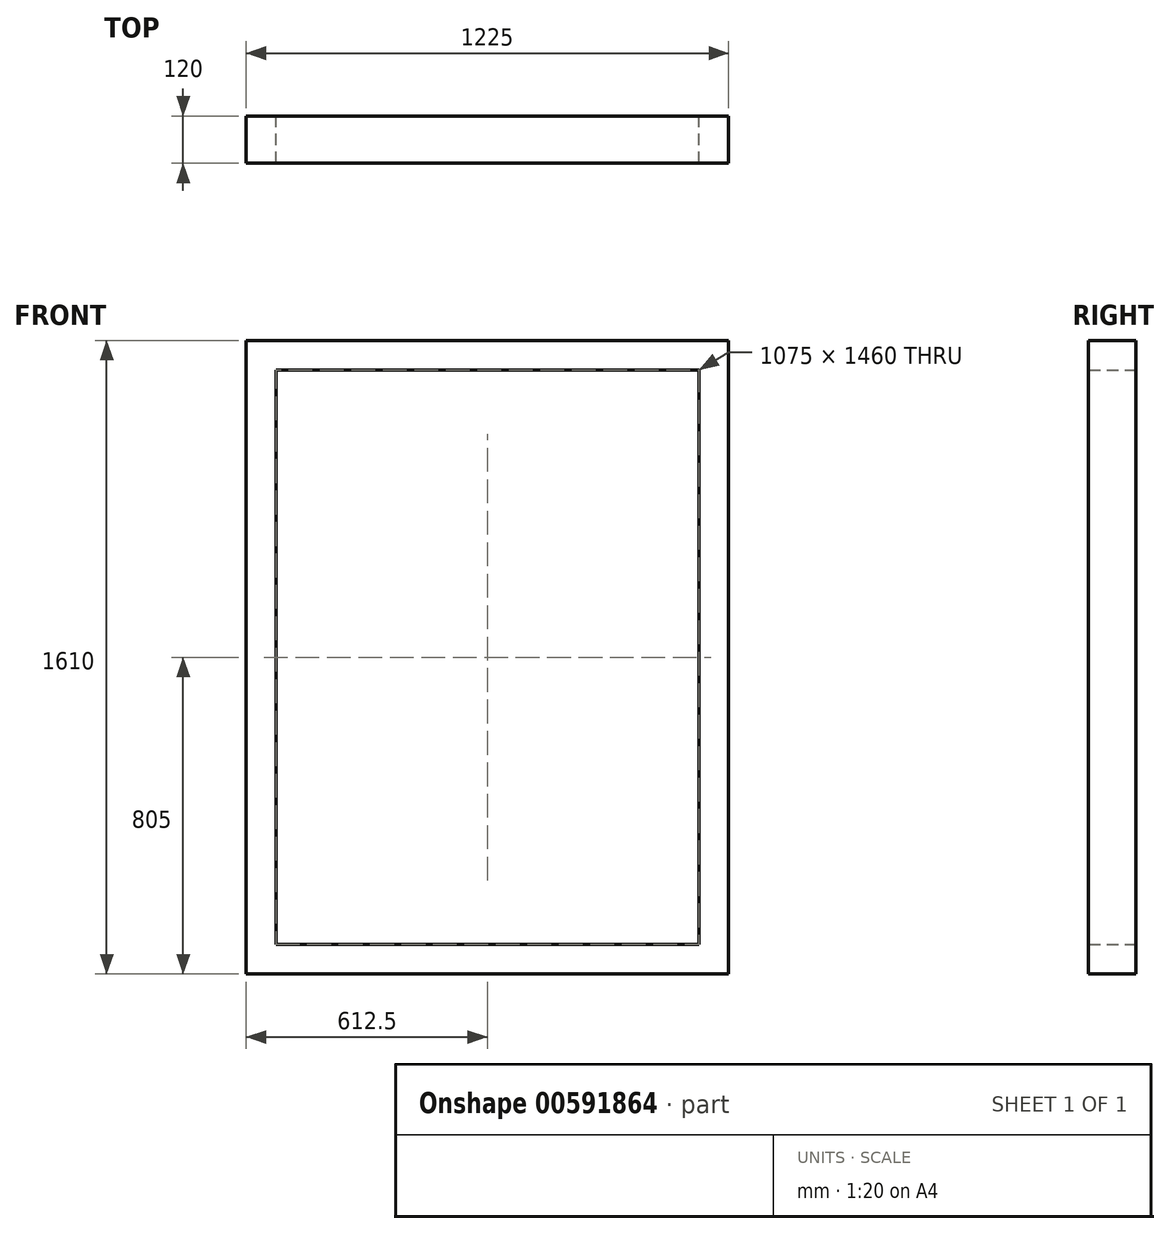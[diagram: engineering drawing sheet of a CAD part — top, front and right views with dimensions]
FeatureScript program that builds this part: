
annotation { "Feature Type Name" : "Feature", "Feature Type Description" : "" }
export const myFeature = defineFeature(function(context is Context, id is Id, definition is map)
    precondition{}
    {
        {
            var Q0;
            Q0=qCreatedBy(makeId("Front.planeOp"),FACE);
            var sketch = newSketch(context, id + "F0", { "sketchPlane" : qUnion([Q0])});
            skLineSegment(sketch, "E0.bottom", {"start": v(0, 0) * mm, "end": v(1225, 0) * mm});
            skLineSegment(sketch, "E0.top", {"start": v(0, 1610) * mm, "end": v(1225, 1610) * mm});
            skLineSegment(sketch, "E0.left", {"start": v(0, 0) * mm, "end": v(0, 1610) * mm});
            skLineSegment(sketch, "E0.right", {"start": v(1225, 0) * mm, "end": v(1225, 1610) * mm});
            skLineSegment(sketch, "E1.0", {"start": v(75, 1535) * mm, "end": v(1150, 1535) * mm});
            skLineSegment(sketch, "E1.1", {"start": v(75, 75) * mm, "end": v(75, 1535) * mm});
            skLineSegment(sketch, "E1.2", {"start": v(75, 75) * mm, "end": v(1150, 75) * mm});
            skLineSegment(sketch, "E1.3", {"start": v(1150, 75) * mm, "end": v(1150, 1535) * mm});
            skSolve(sketch);
        }
        {
            var Q0;
            Q0 = qSketchRegion(id + "F0", true);
            extrude(context, id + "F1", {"entities" : qUnion([Q0]), "depth" : 120 * mm, "offsetDistance" : 25 * mm});
        }
    });
